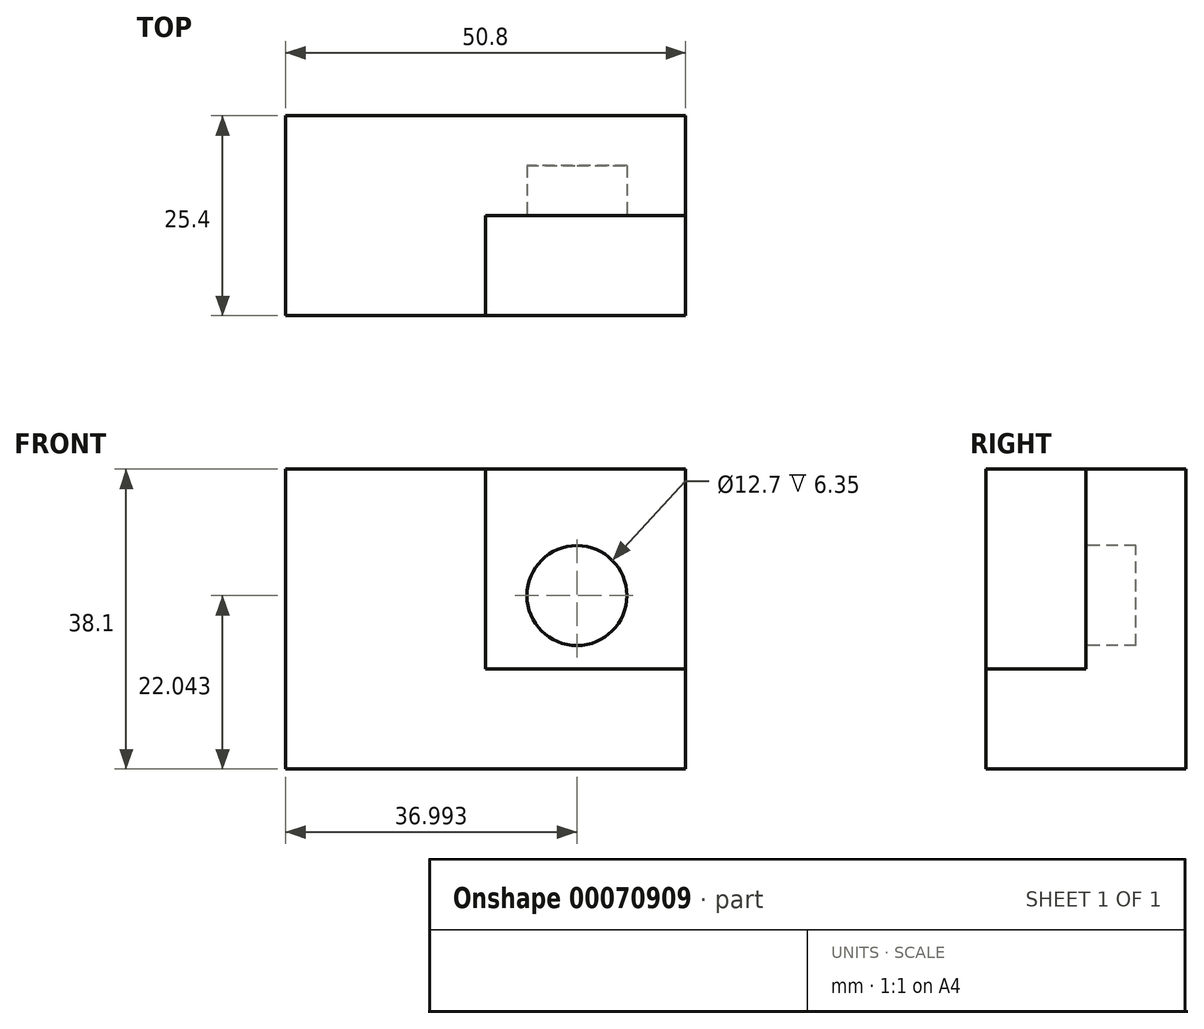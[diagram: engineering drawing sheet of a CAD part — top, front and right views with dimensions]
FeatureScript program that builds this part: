
annotation { "Feature Type Name" : "Feature", "Feature Type Description" : "" }
export const myFeature = defineFeature(function(context is Context, id is Id, definition is map)
    precondition{}
    {
        {
            var Q0;
            Q0=qCreatedBy(makeId("Front.planeOp"),FACE);
            var sketch = newSketch(context, id + "F0", { "sketchPlane" : qUnion([Q0])});
            skLineSegment(sketch, "E0.bottom", {"start": v(-19.62, 22.43) * mm, "end": v(31.18, 22.43) * mm});
            skLineSegment(sketch, "E0.top", {"start": v(-19.62, -15.67) * mm, "end": v(31.18, -15.67) * mm});
            skLineSegment(sketch, "E0.left", {"start": v(-19.62, 22.43) * mm, "end": v(-19.62, -15.67) * mm});
            skLineSegment(sketch, "E0.right", {"start": v(31.18, 22.43) * mm, "end": v(31.18, -15.67) * mm});
            skSolve(sketch);
        }
        {
            var Q0;
            Q0 = qSketchRegion(id + "F0", true);
            extrude(context, id + "F1", {"entities" : qUnion([Q0]), "depth" : 25.4 * mm});
        }
        {
            var Q0;
            Q0=makeQuery(id+"F1.opExtrude","SWEPT_FACE",FACE,{"disambiguationData":[OSD([sQuery(id+"F0.wireOp",EDGE,"E0.bottom")])]});
            var sketch = newSketch(context, id + "F2", { "sketchPlane" : qUnion([Q0])});
            skLineSegment(sketch, "E1.bottom", {"start": v(5.78, -25.4) * mm, "end": v(31.18, -25.4) * mm});
            skLineSegment(sketch, "E1.top", {"start": v(5.78, -12.7) * mm, "end": v(31.18, -12.7) * mm});
            skLineSegment(sketch, "E1.left", {"start": v(5.78, -25.4) * mm, "end": v(5.78, -12.7) * mm});
            skLineSegment(sketch, "E1.right", {"start": v(31.18, -25.4) * mm, "end": v(31.18, -12.7) * mm});
            skSolve(sketch);
        }
        {
            var Q0;
            Q0 = qSketchRegion(id + "F2", true);
            extrude(context, id + "F3", {"entities" : qUnion([Q0]), "operationType" : NewBodyOperationType.REMOVE, "oppositeDirection" : true, "depth" : 25.4 * mm});
        }
        {
            var Q0;
            Q0=makeQuery(id+"F3.boolean.opBoolean","COPY",FACE,{"derivedFrom":makeQuery(id+"F3.opExtrude","SWEPT_FACE",FACE,{"disambiguationData":[OSD([sQuery(id+"F2.wireOp",EDGE,"E1.top")])]})});
            var sketch = newSketch(context, id + "F4", { "sketchPlane" : qUnion([Q0])});
            skCircle(sketch, "E2", {"center": v(17.37, 6.37) * mm, "radius": 6.35 * mm});
            skSolve(sketch);
        }
        {
            var Q0;
            Q0=makeQuery(id+"F4.imprint","IMPRINT",FACE,{"disambiguationData":[TD([[makeQuery(id+"F4.imprint","IMPRINT",EDGE,{"derivedFrom":sQuery(id+"F4.wireOp",EDGE,"E2")}),1.0]])]});
            extrude(context, id + "F5", {"entities" : qUnion([Q0]), "operationType" : NewBodyOperationType.REMOVE, "oppositeDirection" : true, "depth" : 6.35 * mm});
        }
    });
